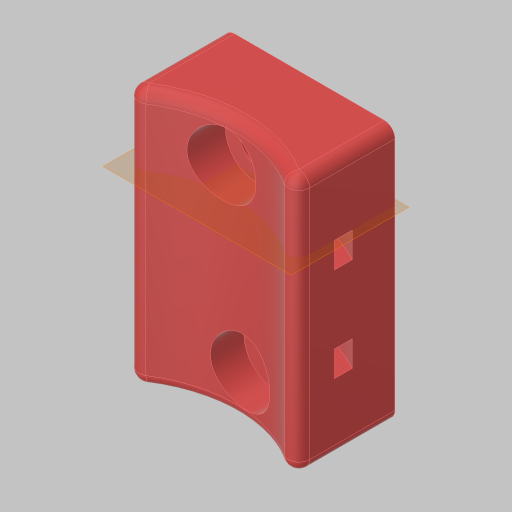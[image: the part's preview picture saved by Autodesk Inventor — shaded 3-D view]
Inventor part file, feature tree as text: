
AUTODESK INVENTOR PART (.ipt)
format: ipt  version: 2023.5 (Build 275446000, 446)  size: 202,240 bytes
history: native  units: in
note: dims shown in document units (in); Inventor stores cm internally (conversion verified against a paired STEP export)
features: sketch x4, extrude x3, plane x2, hole x1, mirror x1, fillet x1, projected_geometry x1
ambient origin geometry x8: Origin, YZ Plane, XZ Plane, XY Plane, X Axis, Y Axis, Z Axis, Center Point
bodies: Solid1 (feature_tree)
feature tree (13):
  sketch  "Sketch1"  dims[d0=1.5in d1=1.0in]
  extrude  "Extrusion1"  Depth=1.0in
  extrude  "Extrusion2"  Depth=0.994in
  plane  "Work Plane1"
  hole  "Hole2"  [1 undecoded]
  plane  "Work Plane2"
  extrude  "Extrusion3"  TaperAngle=0.0deg  [1 undecoded]
  mirror  "Mirror1"
  fillet  "Fillet1"  [1 undecoded]
  sketch  "Sketch2"  dims[d2=0.109in d3=0.994in]
  projected_geometry  "Projected Loop1"
  sketch  "Sketch3"  dims[d4=0.75in d5=0.0in d13=0.75in]
  sketch  "Sketch5"  dims[d14=0.125in d15=0.0in d16=0.0in d17=-0.44in d18=0.201in d19=0.75in d20=0.375in d21=0.19in d22=0.5635in d23=1.0in d24=0.8108in d28=-0.4in d29=0.09in d30=0.25in d31=0.15in d32=0.0in d33=0.0625in]
note: 3 required parameter values undecoded (feature->parameter linkage not recoverable at this tier; creation-order binding heuristic only, values carry confidence <= 0.55)
